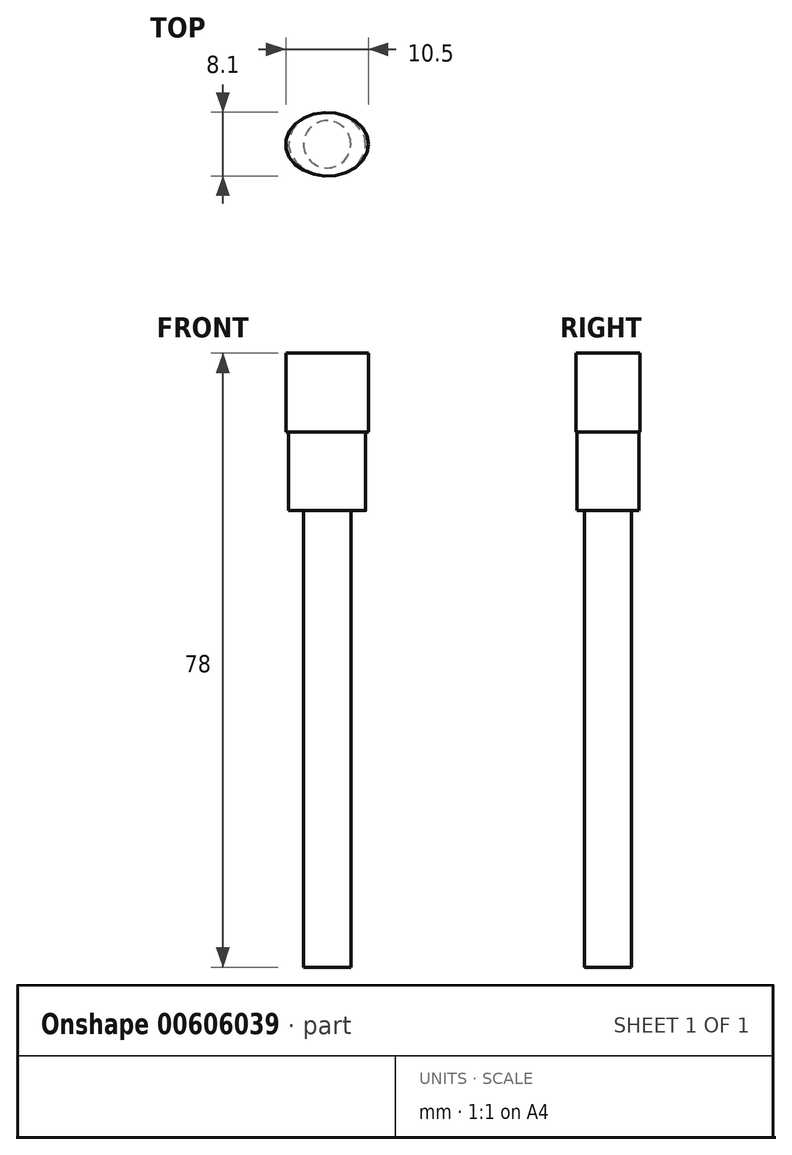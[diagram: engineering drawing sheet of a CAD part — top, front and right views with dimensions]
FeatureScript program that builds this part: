
annotation { "Feature Type Name" : "Feature", "Feature Type Description" : "" }
export const myFeature = defineFeature(function(context is Context, id is Id, definition is map)
    precondition{}
    {
        {
            var Q0;
            Q0=qCreatedBy(makeId("Top.planeOp"),FACE);
            var sketch = newSketch(context, id + "F0", { "sketchPlane" : qUnion([Q0])});
            skEllipse(sketch, "E0", {"center": v(0, 0) * mm, "majorRadius": 4.9 * mm, "minorRadius": 3.95 * mm, "majorAxis": v(1, -0.06)});
            skSolve(sketch);
        }
        {
            var Q0;
            Q0=makeQuery(id+"F0.imprint","IMPRINT",FACE,{"disambiguationData":[TD([[makeQuery(id+"F0.imprint","IMPRINT",EDGE,{"derivedFrom":sQuery(id+"F0.wireOp",EDGE,"E0")}),1.0]])]});
            extrude(context, id + "F1", {"entities" : qUnion([Q0]), "depth" : 10 * mm, "offsetDistance" : 25 * mm});
        }
        {
            var Q0;
            Q0=makeQuery(id+"F1.opExtrude","CAP_FACE",FACE,{"disambiguationData":[OSD([sQuery(id+"F0.wireOp",EDGE,"E0")])],"isStart":false});
            var sketch = newSketch(context, id + "F2", { "sketchPlane" : qUnion([Q0])});
            skEllipse(sketch, "E1", {"center": v(0, 0) * mm, "majorRadius": 5.25 * mm, "minorRadius": 4.05 * mm, "majorAxis": v(1, 0)});
            skSolve(sketch);
        }
        {
            var Q0;
            Q0=qSketchRegion(id+"F2",true);
            extrude(context, id + "F3", {"entities" : qUnion([Q0]), "operationType" : NewBodyOperationType.ADD, "depth" : 10 * mm, "offsetDistance" : 25 * mm});
        }
        {
            var Q0;
            Q0=makeQuery(id+"F1.opExtrude","CAP_FACE",FACE,{"disambiguationData":[OSD([sQuery(id+"F0.wireOp",EDGE,"E0")])],"isStart":true});
            var sketch = newSketch(context, id + "F4", { "sketchPlane" : qUnion([Q0])});
            skCircle(sketch, "E2", {"center": v(0, 0) * mm, "radius": 3 * mm});
            skSolve(sketch);
        }
        {
            var Q0;
            Q0=makeQuery(id+"F4.imprint","IMPRINT",FACE,{"disambiguationData":[TD([[makeQuery(id+"F4.imprint","IMPRINT",EDGE,{"derivedFrom":sQuery(id+"F4.wireOp",EDGE,"E2")}),1.0]])]});
            extrude(context, id + "F5", {"entities" : qUnion([Q0]), "operationType" : NewBodyOperationType.ADD, "depth" : 58 * mm, "offsetDistance" : 25 * mm});
        }
    });
